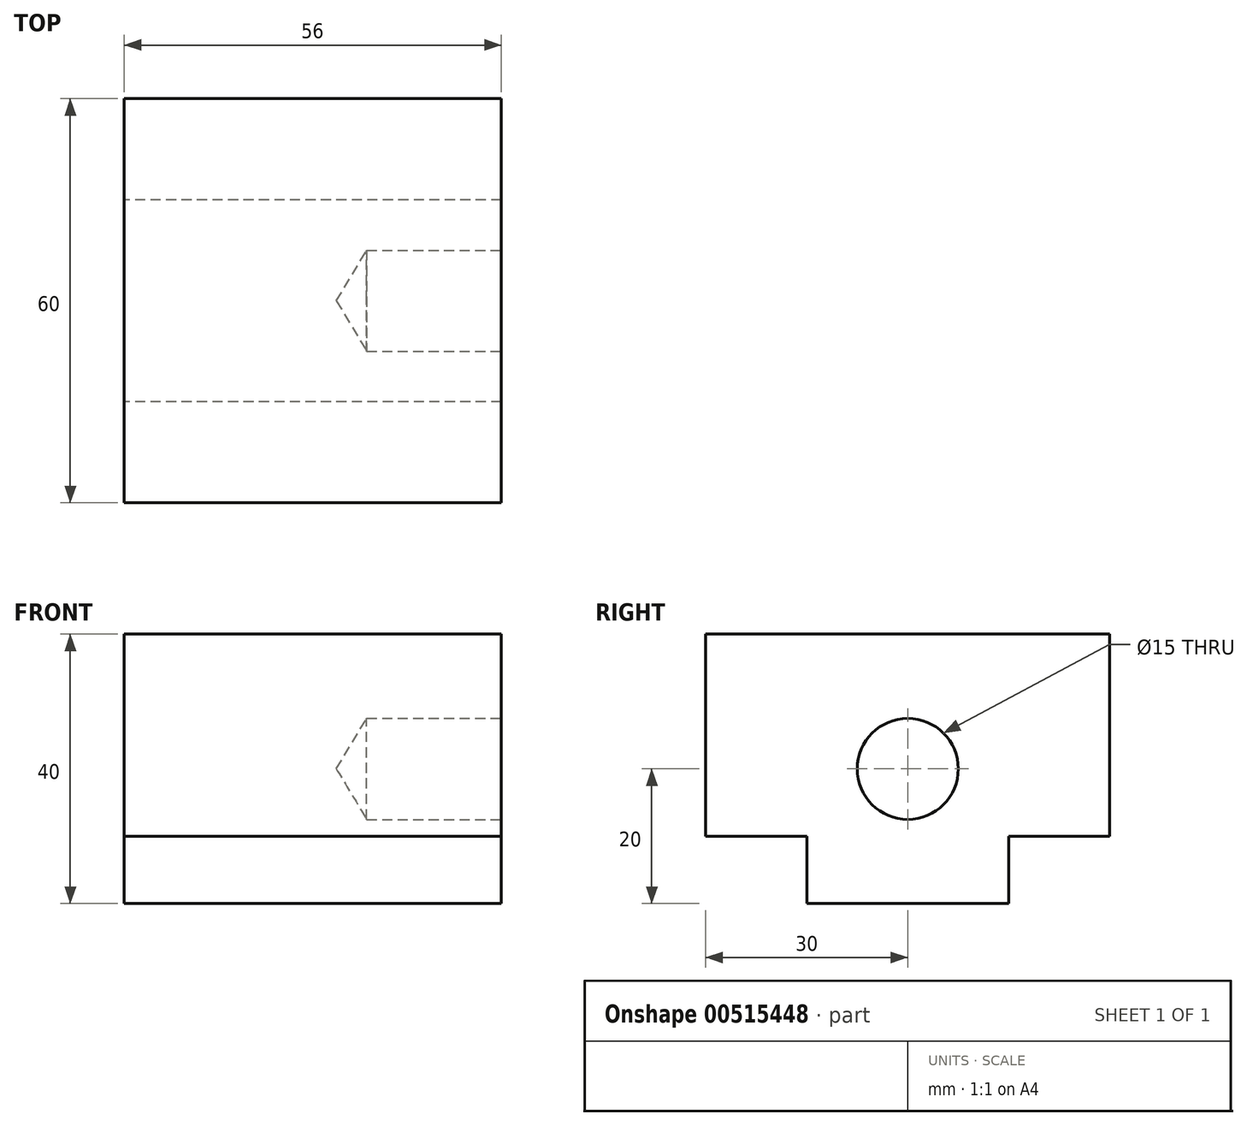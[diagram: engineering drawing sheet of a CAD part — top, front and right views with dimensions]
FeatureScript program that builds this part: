
annotation { "Feature Type Name" : "Feature", "Feature Type Description" : "" }
export const myFeature = defineFeature(function(context is Context, id is Id, definition is map)
    precondition{}
    {
        {
            var Q0;
            Q0=qCreatedBy(makeId("Right.planeOp"),FACE);
            var sketch = newSketch(context, id + "F0", { "sketchPlane" : qUnion([Q0])});
            skLineSegment(sketch, "E0", {"start": v(0, 0) * mm, "end": v(15, 0) * mm});
            skLineSegment(sketch, "E1", {"start": v(15, 0) * mm, "end": v(15, 10) * mm});
            skLineSegment(sketch, "E2", {"start": v(15, 10) * mm, "end": v(30, 10) * mm});
            skLineSegment(sketch, "E3", {"start": v(30, 10) * mm, "end": v(30, 40) * mm});
            skLineSegment(sketch, "E4", {"start": v(30, 40) * mm, "end": v(0, 40) * mm});
            skLineSegment(sketch, "E5", {"start": v(0, 40) * mm, "end": v(0, 0) * mm, "construction": true});
            skLineSegment(sketch, "E6.MirrorCS", {"start": v(-30, 40) * mm, "end": v(0, 40) * mm});
            skLineSegment(sketch, "E7.MirrorCS", {"start": v(-15, 10) * mm, "end": v(-30, 10) * mm});
            skLineSegment(sketch, "E8.MirrorCS", {"start": v(-15, 0) * mm, "end": v(-15, 10) * mm});
            skLineSegment(sketch, "E9.MirrorCS", {"start": v(-30, 10) * mm, "end": v(-30, 40) * mm});
            skLineSegment(sketch, "E10.MirrorCS", {"start": v(0, 0) * mm, "end": v(-15, 0) * mm});
            skSolve(sketch);
        }
        {
            var Q0;
            Q0=makeQuery(id+"F0.imprint","IMPRINT",FACE,{"disambiguationData":[TD([[makeQuery(id+"F0.imprint","IMPRINT",EDGE,{"derivedFrom":sQuery(id+"F0.wireOp",EDGE,"E0")}),1.0]])]});
            extrude(context, id + "F1", {"entities" : qUnion([Q0]), "depth" : 56 * mm, "offsetDistance" : 25 * mm});
        }
        {
            var Q0;
            Q0=makeQuery(id+"F1.opExtrude","CAP_FACE",FACE,{"disambiguationData":[OSD([sQuery(id+"F0.wireOp",EDGE,"E0"),sQuery(id+"F0.wireOp",EDGE,"E1"),sQuery(id+"F0.wireOp",EDGE,"E2"),sQuery(id+"F0.wireOp",EDGE,"E3"),sQuery(id+"F0.wireOp",EDGE,"E4"),sQuery(id+"F0.wireOp",EDGE,"E6.MirrorCS"),sQuery(id+"F0.wireOp",EDGE,"E7.MirrorCS"),sQuery(id+"F0.wireOp",EDGE,"E8.MirrorCS"),sQuery(id+"F0.wireOp",EDGE,"E9.MirrorCS"),sQuery(id+"F0.wireOp",EDGE,"E10.MirrorCS")])],"isStart":false});
            var sketch = newSketch(context, id + "F2", { "sketchPlane" : qUnion([Q0])});
            skPoint(sketch, "E11", {"position": v(0, 20) * mm});
            skSolve(sketch);
        }
        {
            var Q0;
            Q0=sQuery(id+"F2.wireOp",VERTEX,"E11");
            var Q1;
            Q1=makeQuery(id+"F1.opExtrude","SWEPT_BODY",BODY,{"disambiguationData":[OSD([sQuery(id+"F0.wireOp",EDGE,"E0"),sQuery(id+"F0.wireOp",EDGE,"E1"),sQuery(id+"F0.wireOp",EDGE,"E2"),sQuery(id+"F0.wireOp",EDGE,"E3"),sQuery(id+"F0.wireOp",EDGE,"E4"),sQuery(id+"F0.wireOp",EDGE,"E6.MirrorCS"),sQuery(id+"F0.wireOp",EDGE,"E7.MirrorCS"),sQuery(id+"F0.wireOp",EDGE,"E8.MirrorCS"),sQuery(id+"F0.wireOp",EDGE,"E9.MirrorCS"),sQuery(id+"F0.wireOp",EDGE,"E10.MirrorCS")])]});
            hole(context, id + "F3", {"style" : HoleStyle.SIMPLE, "endStyle" : HoleEndStyle.BLIND, "holeDiameter" : 15 * mm, "holeDepth" : 20 * mm, "isTappedThrough" : true, "tappedDepth" : 12 * mm, "tapClearance" : 3, "locations" : qUnion([Q0]), "scope" : qUnion([Q1])});
        }
    });
